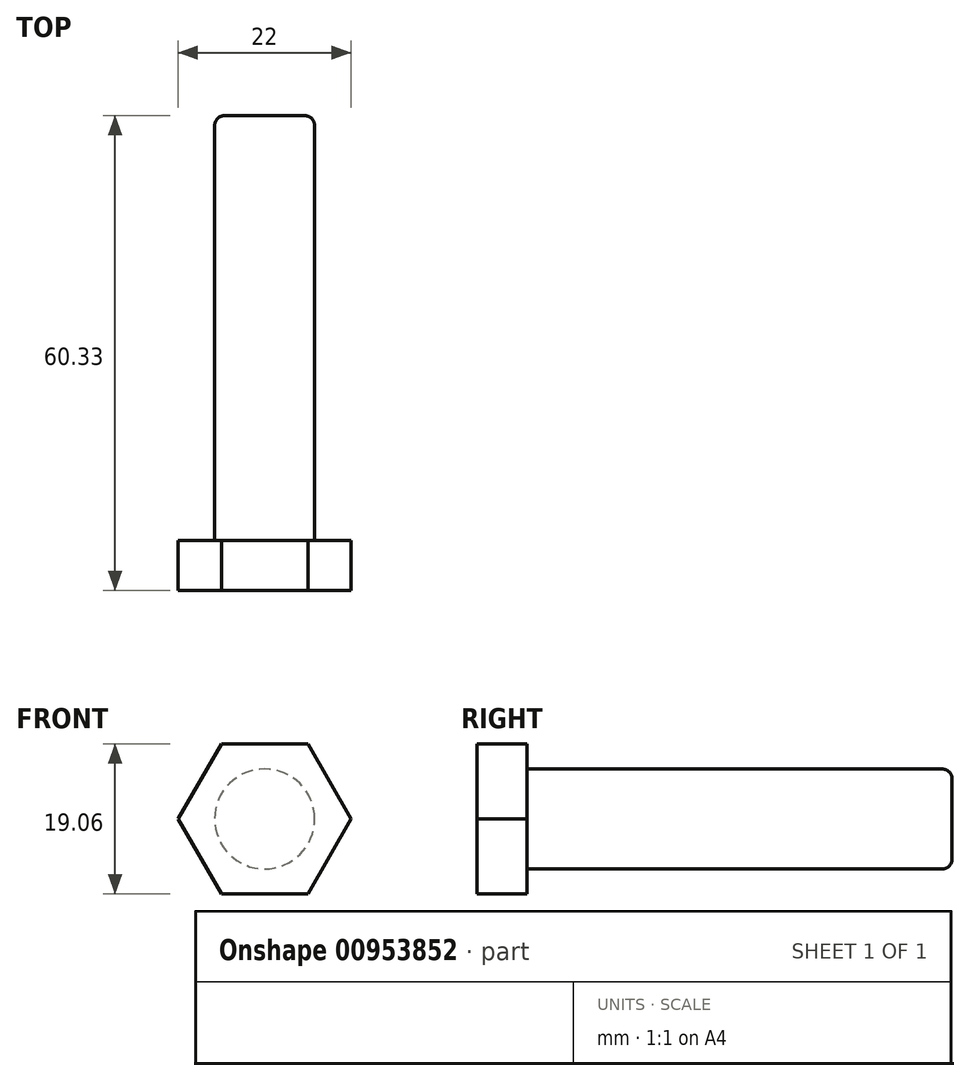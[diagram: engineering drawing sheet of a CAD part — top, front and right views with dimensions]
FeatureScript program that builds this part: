
annotation { "Feature Type Name" : "Feature", "Feature Type Description" : "" }
export const myFeature = defineFeature(function(context is Context, id is Id, definition is map)
    precondition{}
    {
        {
            var Q0;
            Q0=qCreatedBy(makeId("Front.planeOp"),FACE);
            var sketch = newSketch(context, id + "F0", { "sketchPlane" : qUnion([Q0])});
            skCircle(sketch, "E0.cCircle", {"center": v(0, 0) * mm, "radius": 9.52 * mm, "construction": true});
            skLineSegment(sketch, "E0.0", {"start": v(-11, 0) * mm, "end": v(-5.5, 9.53) * mm});
            skLineSegment(sketch, "E0.1", {"start": v(-5.5, 9.53) * mm, "end": v(5.5, 9.52) * mm});
            skLineSegment(sketch, "E0.2", {"start": v(5.5, 9.53) * mm, "end": v(11, 0) * mm});
            skLineSegment(sketch, "E0.3", {"start": v(11, 0) * mm, "end": v(5.5, -9.52) * mm});
            skLineSegment(sketch, "E0.4", {"start": v(5.5, -9.53) * mm, "end": v(-5.5, -9.52) * mm});
            skLineSegment(sketch, "E0.5", {"start": v(-5.5, -9.53) * mm, "end": v(-11, 0) * mm});
            skPoint(sketch, "E0.0.midPoint", {"position": v(-8.25, 4.76) * mm});
            skSolve(sketch);
        }
        {
            var Q0;
            Q0 = qSketchRegion(id + "F0", true);
            extrude(context, id + "F1", {"entities" : qUnion([Q0]), "depth" : 6.35 * mm, "offsetDistance" : 25.4 * mm});
        }
        {
            var Q0;
            Q0=makeQuery(id+"F1.opExtrude","CAP_FACE",FACE,{"disambiguationData":[OSD([sQuery(id+"F0.wireOp",EDGE,"E0.0"),sQuery(id+"F0.wireOp",EDGE,"E0.1"),sQuery(id+"F0.wireOp",EDGE,"E0.2"),sQuery(id+"F0.wireOp",EDGE,"E0.3"),sQuery(id+"F0.wireOp",EDGE,"E0.4"),sQuery(id+"F0.wireOp",EDGE,"E0.5")])],"isStart":true});
            var sketch = newSketch(context, id + "F2", { "sketchPlane" : qUnion([Q0])});
            skCircle(sketch, "E1", {"center": v(0, 0) * mm, "radius": 6.35 * mm});
            skSolve(sketch);
        }
        {
            var Q0;
            Q0 = qSketchRegion(id + "F2", true);
            extrude(context, id + "F3", {"entities" : qUnion([Q0]), "operationType" : NewBodyOperationType.ADD, "depth" : 53.97 * mm, "offsetDistance" : 25.4 * mm});
        }
        {
            var Q0;
            Q0=makeQuery(id+"F3.opExtrude","CAP_EDGE",EDGE,{"disambiguationData":[OSD([sQuery(id+"F2.wireOp",EDGE,"E1")])],"isStart":false});
            fillet(context, id + "F4", {"entities" : qUnion([Q0]), "radius" : 1.27 * mm, "tangentPropagation" : true, "allowEdgeOverflow" : false});
        }
    });
